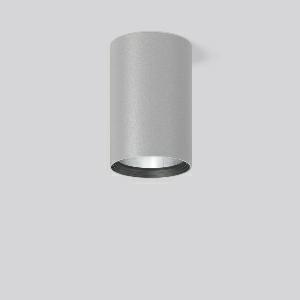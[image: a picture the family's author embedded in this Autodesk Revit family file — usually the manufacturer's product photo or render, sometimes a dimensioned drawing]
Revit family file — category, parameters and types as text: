
# Revit family: heledon_maxi_a_931219_004_2_d890
name_source: partatom
category: Lighting Fixtures
units: mm (PartAtom-declared; Revit-internal decimal feet)

## family parameters
Cut with Voids When Loaded = No
Host = Face
Light Source = No
Part Type = Normal
Room Calculation Point = No
Round Connector Dimension = Use Diameter
Shared = No

## types (1)
- HELEDON maxi A (1 x LED Modul 927, 3050 lm, 2700)
    Apparent Load = 25 VA
    Approval mark = CE
    CIE Flux Codes = 97 100 100 100 100
    Color Rendering = 92
    Color Temperature = 2700
    Default Elevation = 1800 mm
    Description = Series: HELEDON maxi
Cylindrical surface-mounted downlight. Housing: die-cast aluminium, powder-coated. Internal ceiling frame polycarbonate with bayonet mounting. Black plastic ring and recessed LED to prevent glare from the side. Optical assembly with reflector made of MIRO-Silver with 98% total light reflection for outstanding efficiency - can be changed without tools. Best colour rendering index Ra>90. Suitable for Ceiling mounting. Easy installation with a separate ceiling frame with bayonet mounting and plug connection. Driver integrated. Connected via plug-in connector. High quality converter without flickering and stroboscopic effect. The following accessories can be mounted without use of tools: interchangeable lenses, decorative glasses, honeycomb louvre, clear and frosted diffusers, white interchangeable plastic ring. 
Colour: silver
Diameter: 123 mm
Height: 183 mm
Lamp: LED
Socket: without socket
Colour temperature: 2700K
Colour rendering index (CRI): 92
System power: 25 W
Rated luminous flux: 3050 lm
Luminous efficiency: 122 lm/W
Control gear: Regulated power supply
Protection class: I
Type of protection: IP 20
    Height = 183 mm
    Lamp = 1 x LED Modul 927
    Lamp Light Flux = 3050 lm
    Lamp count = 1
    Length = 123 mm
    Lifetime = 50000 h
    Luminous efficacy = 122 lm/W
    Manufacturer = RZB
    ModVariant = No
    Model = 931219.004.2
    Mounting Place = Ceiling
    Mounting Type = Surface mounted
    Number of Poles = 1
    OnlyDefault = Yes
    Power Factor = 1
    Product Name = HELEDON maxi A
    Product group = Surface mounted downlights
    ProductGroupID = 302
    Protection Class = Protection class I
    Protection Degree = IP 20
    RLX_Detail_Level = 1
    RLX_Emergency_Light_Flux = 0 lm
    RLX_Emergency_Type = 0
    RLX_Emergency_Type_DB = No
    RlxData = <blob elided: 100513 chars, md5=d1d6a1e3>
    Socket = socket
    Standby Power = 0 W
    System Light Flux = 3050 lm
    System Power = 25 W
    Type Comments = Product without accessories
    Type Image = 931192.004.jpg
    URL = http://relux.com
    VarID = ---
    Voltage = 230 V
    Voltage Range = 220-240 V
    Weight = 0.00 kg
    Width = 0 mm  [stored 0 ft]

note: [stored X ft] marks values corroborated as IEEE doubles in the binary element streams (Revit-internal decimal feet)

## geometry (parser evidence)
native form markers: Blend x4, Sweep x10
no freeform markers — native parametric forms only
